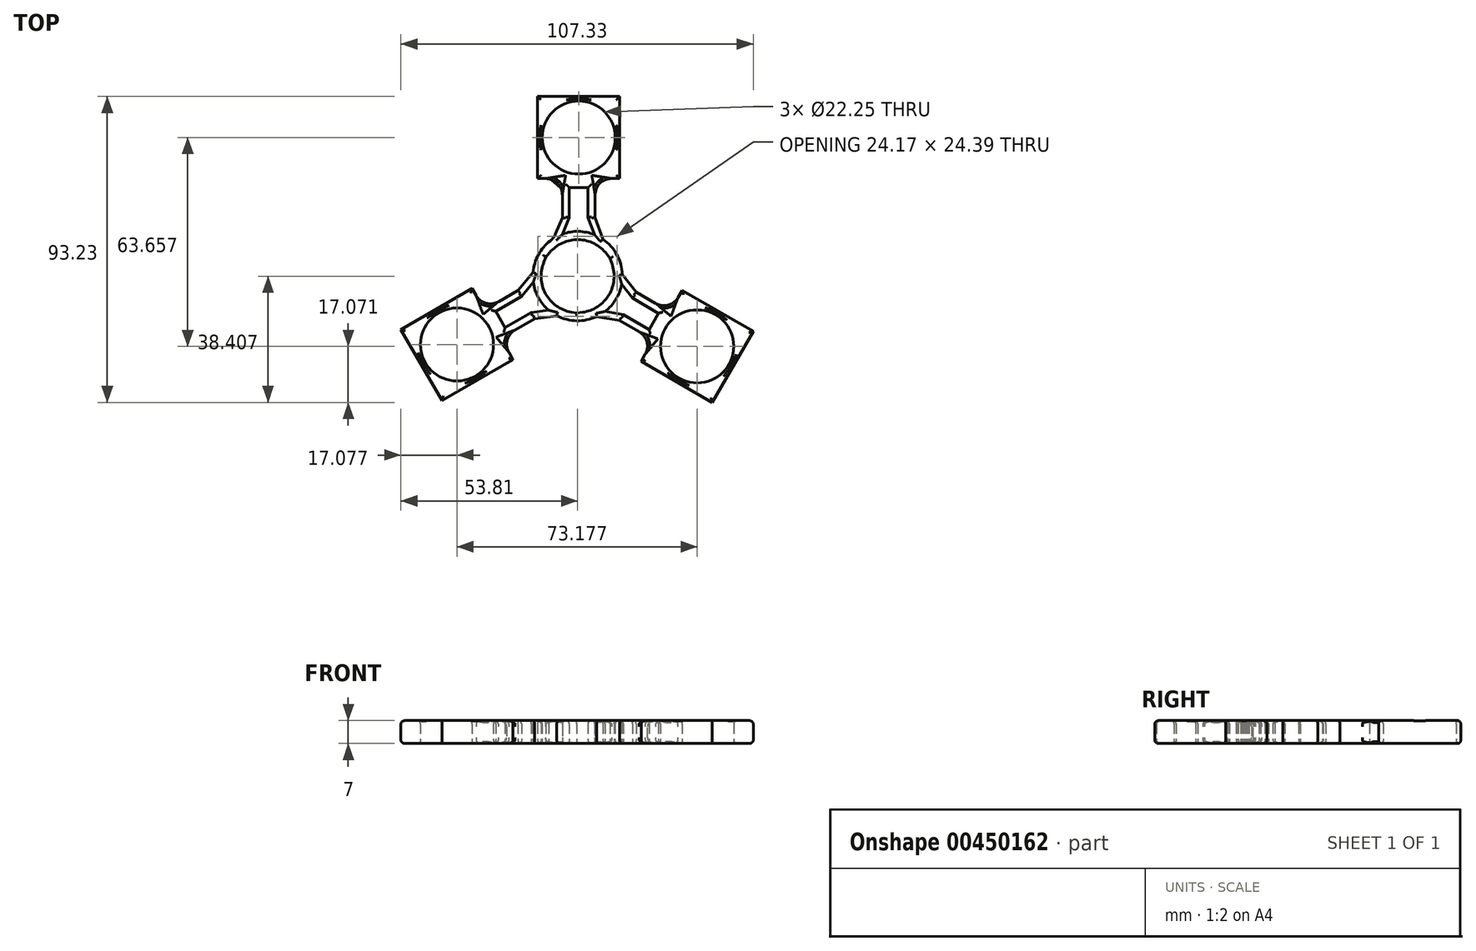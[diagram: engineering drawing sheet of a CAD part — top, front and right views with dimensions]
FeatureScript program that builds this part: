
annotation { "Feature Type Name" : "Feature", "Feature Type Description" : "" }
export const myFeature = defineFeature(function(context is Context, id is Id, definition is map)
    precondition{}
    {
        {
            var Q0;
            Q0=qCreatedBy(makeId("Top.planeOp"),FACE);
            var sketch = newSketch(context, id + "F0", { "sketchPlane" : qUnion([Q0])});
            skCircle(sketch, "E0", {"center": v(0, 0) * mm, "radius": 11.13 * mm});
            skCircle(sketch, "E1.0.1.0", {"center": v(0.33, 42.25) * mm, "radius": 11.13 * mm});
            skLineSegment(sketch, "E2.bottom", {"start": v(12.83, 54.75) * mm, "end": v(-12.17, 54.75) * mm});
            skLineSegment(sketch, "E2.top", {"start": v(12.83, 29.75) * mm, "end": v(-12.17, 29.75) * mm});
            skLineSegment(sketch, "E2.left", {"start": v(12.83, 54.75) * mm, "end": v(12.83, 29.75) * mm});
            skLineSegment(sketch, "E2.right", {"start": v(-12.17, 54.75) * mm, "end": v(-12.17, 29.75) * mm});
            skLineSegment(sketch, "E3", {"start": v(-4.67, 29.75) * mm, "end": v(-4.67, 17.87) * mm});
            skLineSegment(sketch, "E4", {"start": v(-4.67, 17.87) * mm, "end": v(-10.29, 4.24) * mm});
            skLineSegment(sketch, "E5", {"start": v(5.33, 29.75) * mm, "end": v(5.33, 17.9) * mm});
            skLineSegment(sketch, "E6", {"start": v(5.33, 17.9) * mm, "end": v(10.45, 3.8) * mm});
            skLineSegment(sketch, "E7", {"start": v(-2.54, 27) * mm, "end": v(-2.54, 17.8) * mm});
            skLineSegment(sketch, "E8", {"start": v(-2.54, 17.8) * mm, "end": v(-4.82, 12.26) * mm});
            skLineSegment(sketch, "E9", {"start": v(5.25, 12.26) * mm, "end": v(3.2, 17.9) * mm});
            skLineSegment(sketch, "E10", {"start": v(3.2, 17.9) * mm, "end": v(3.2, 27) * mm});
            skLineSegment(sketch, "E11", {"start": v(3.2, 27) * mm, "end": v(-2.54, 27) * mm});
            skCircle(sketch, "E12", {"center": v(0, 0) * mm, "radius": 13.63 * mm});
            skCircle(sketch, "E13.1.0", {"center": v(-36.75, -20.84) * mm, "radius": 11.13 * mm});
            skLineSegment(sketch, "E13.1.1", {"start": v(-28.43, -10.26) * mm, "end": v(-18.16, -4.33) * mm});
            skLineSegment(sketch, "E13.1.2", {"start": v(-32.18, -3.76) * mm, "end": v(-19.68, -25.42) * mm});
            skLineSegment(sketch, "E13.1.3", {"start": v(-53.83, -16.26) * mm, "end": v(-32.18, -3.76) * mm});
            skLineSegment(sketch, "E13.1.4", {"start": v(-41.33, -37.92) * mm, "end": v(-19.68, -25.42) * mm});
            skLineSegment(sketch, "E13.1.5", {"start": v(-53.83, -16.26) * mm, "end": v(-41.33, -37.92) * mm});
            skLineSegment(sketch, "E13.1.6", {"start": v(-22.11, -15.7) * mm, "end": v(-14.15, -11.1) * mm});
            skLineSegment(sketch, "E13.1.7", {"start": v(-17.1, -6.18) * mm, "end": v(-24.98, -10.73) * mm});
            skLineSegment(sketch, "E13.1.8", {"start": v(-24.98, -10.73) * mm, "end": v(-22.11, -15.7) * mm});
            skLineSegment(sketch, "E13.1.9", {"start": v(-13.24, -1.58) * mm, "end": v(-17.1, -6.18) * mm});
            skLineSegment(sketch, "E13.1.10", {"start": v(-14.15, -11.1) * mm, "end": v(-8.2, -10.3) * mm});
            skLineSegment(sketch, "E13.1.12", {"start": v(-13.14, -12.98) * mm, "end": v(1.47, -11.03) * mm});
            skLineSegment(sketch, "E13.1.13", {"start": v(-18.16, -4.33) * mm, "end": v(-8.52, 7.15) * mm});
            skLineSegment(sketch, "E13.1.14", {"start": v(-23.43, -18.92) * mm, "end": v(-13.14, -12.98) * mm});
            skCircle(sketch, "E13.2.0", {"center": v(36.42, -21.4) * mm, "radius": 11.13 * mm});
            skLineSegment(sketch, "E13.2.1", {"start": v(23.1, -19.49) * mm, "end": v(12.84, -13.56) * mm});
            skLineSegment(sketch, "E13.2.2", {"start": v(19.35, -25.98) * mm, "end": v(31.85, -4.33) * mm});
            skLineSegment(sketch, "E13.2.3", {"start": v(41, -38.48) * mm, "end": v(19.35, -25.98) * mm});
            skLineSegment(sketch, "E13.2.4", {"start": v(53.5, -16.83) * mm, "end": v(31.85, -4.33) * mm});
            skLineSegment(sketch, "E13.2.5", {"start": v(41, -38.48) * mm, "end": v(53.5, -16.83) * mm});
            skLineSegment(sketch, "E13.2.6", {"start": v(24.65, -11.3) * mm, "end": v(16.69, -6.7) * mm});
            skLineSegment(sketch, "E13.2.7", {"start": v(13.9, -11.72) * mm, "end": v(21.78, -16.27) * mm});
            skLineSegment(sketch, "E13.2.8", {"start": v(21.78, -16.27) * mm, "end": v(24.65, -11.3) * mm});
            skLineSegment(sketch, "E13.2.9", {"start": v(8, -10.68) * mm, "end": v(13.9, -11.72) * mm});
            skLineSegment(sketch, "E13.2.10", {"start": v(16.69, -6.7) * mm, "end": v(13.03, -1.96) * mm});
            skLineSegment(sketch, "E13.2.12", {"start": v(17.81, -4.9) * mm, "end": v(8.81, 6.8) * mm});
            skLineSegment(sketch, "E13.2.13", {"start": v(12.84, -13.56) * mm, "end": v(-1.93, -10.96) * mm});
            skLineSegment(sketch, "E13.2.14", {"start": v(28.1, -10.83) * mm, "end": v(17.81, -4.9) * mm});
            skSolve(sketch);
        }
        {
            var Q0;
            Q0 = qSketchRegion(id + "F0", true);
            extrude(context, id + "F1", {"entities" : qUnion([Q0]), "depth" : 7 * mm, "offsetDistance" : 25 * mm});
        }
        {
            var Q0;
            Q0=makeQuery(id+"F1.opExtrude","SWEPT_EDGE",EDGE,{"disambiguationData":[OSD([sQuery(id+"F0.wireOp",EDGE,"E4"),sQuery(id+"F0.wireOp",EDGE,"E12")])]});
            fillet(context, id + "F2", {"entities" : qUnion([Q0]), "radius" : 5 * mm, "tangentPropagation" : true, "allowEdgeOverflow" : false});
        }
        {
            var Q0;
            Q0=makeQuery(id+"F1.opExtrude","CAP_FACE",FACE,{"disambiguationData":[OSD([sQuery(id+"F0.wireOp",EDGE,"E0"),sQuery(id+"F0.wireOp",EDGE,"E1.0.1.0"),sQuery(id+"F0.wireOp",EDGE,"E2.bottom"),sQuery(id+"F0.wireOp",EDGE,"E2.top"),sQuery(id+"F0.wireOp",EDGE,"E2.left"),sQuery(id+"F0.wireOp",EDGE,"E2.right"),sQuery(id+"F0.wireOp",EDGE,"E3"),sQuery(id+"F0.wireOp",EDGE,"E4"),sQuery(id+"F0.wireOp",EDGE,"E5"),sQuery(id+"F0.wireOp",EDGE,"E6"),sQuery(id+"F0.wireOp",EDGE,"E7"),sQuery(id+"F0.wireOp",EDGE,"E8"),sQuery(id+"F0.wireOp",EDGE,"E9"),sQuery(id+"F0.wireOp",EDGE,"E10"),sQuery(id+"F0.wireOp",EDGE,"E11"),sQuery(id+"F0.wireOp",EDGE,"E12"),sQuery(id+"F0.wireOp",EDGE,"E13.1.0"),sQuery(id+"F0.wireOp",EDGE,"E13.1.1"),sQuery(id+"F0.wireOp",EDGE,"E13.1.2"),sQuery(id+"F0.wireOp",EDGE,"E13.1.3"),sQuery(id+"F0.wireOp",EDGE,"E13.1.4"),sQuery(id+"F0.wireOp",EDGE,"E13.1.5"),sQuery(id+"F0.wireOp",EDGE,"E13.1.6"),sQuery(id+"F0.wireOp",EDGE,"E13.1.7"),sQuery(id+"F0.wireOp",EDGE,"E13.1.8"),sQuery(id+"F0.wireOp",EDGE,"E13.1.9"),sQuery(id+"F0.wireOp",EDGE,"E13.1.10"),sQuery(id+"F0.wireOp",EDGE,"E13.1.12"),sQuery(id+"F0.wireOp",EDGE,"E13.1.13"),sQuery(id+"F0.wireOp",EDGE,"E13.1.14"),sQuery(id+"F0.wireOp",EDGE,"E13.2.0"),sQuery(id+"F0.wireOp",EDGE,"E13.2.1"),sQuery(id+"F0.wireOp",EDGE,"E13.2.2"),sQuery(id+"F0.wireOp",EDGE,"E13.2.3"),sQuery(id+"F0.wireOp",EDGE,"E13.2.4"),sQuery(id+"F0.wireOp",EDGE,"E13.2.5"),sQuery(id+"F0.wireOp",EDGE,"E13.2.6"),sQuery(id+"F0.wireOp",EDGE,"E13.2.7"),sQuery(id+"F0.wireOp",EDGE,"E13.2.8"),sQuery(id+"F0.wireOp",EDGE,"E13.2.9"),sQuery(id+"F0.wireOp",EDGE,"E13.2.10"),sQuery(id+"F0.wireOp",EDGE,"E13.2.12"),sQuery(id+"F0.wireOp",EDGE,"E13.2.13"),sQuery(id+"F0.wireOp",EDGE,"E13.2.14")])],"isStart":false});
            fillet(context, id + "F3", {"entities" : qUnion([Q0]), "radius" : 1 * mm, "tangentPropagation" : true, "allowEdgeOverflow" : false});
        }
        {
            var Q0;
            Q0=makeQuery(id+"F1.opExtrude","CAP_FACE",FACE,{"disambiguationData":[OSD([sQuery(id+"F0.wireOp",EDGE,"E0"),sQuery(id+"F0.wireOp",EDGE,"E1.0.1.0"),sQuery(id+"F0.wireOp",EDGE,"E2.bottom"),sQuery(id+"F0.wireOp",EDGE,"E2.top"),sQuery(id+"F0.wireOp",EDGE,"E2.left"),sQuery(id+"F0.wireOp",EDGE,"E2.right"),sQuery(id+"F0.wireOp",EDGE,"E3"),sQuery(id+"F0.wireOp",EDGE,"E4"),sQuery(id+"F0.wireOp",EDGE,"E5"),sQuery(id+"F0.wireOp",EDGE,"E6"),sQuery(id+"F0.wireOp",EDGE,"E7"),sQuery(id+"F0.wireOp",EDGE,"E8"),sQuery(id+"F0.wireOp",EDGE,"E9"),sQuery(id+"F0.wireOp",EDGE,"E10"),sQuery(id+"F0.wireOp",EDGE,"E11"),sQuery(id+"F0.wireOp",EDGE,"E12"),sQuery(id+"F0.wireOp",EDGE,"E13.1.0"),sQuery(id+"F0.wireOp",EDGE,"E13.1.1"),sQuery(id+"F0.wireOp",EDGE,"E13.1.2"),sQuery(id+"F0.wireOp",EDGE,"E13.1.3"),sQuery(id+"F0.wireOp",EDGE,"E13.1.4"),sQuery(id+"F0.wireOp",EDGE,"E13.1.5"),sQuery(id+"F0.wireOp",EDGE,"E13.1.6"),sQuery(id+"F0.wireOp",EDGE,"E13.1.7"),sQuery(id+"F0.wireOp",EDGE,"E13.1.8"),sQuery(id+"F0.wireOp",EDGE,"E13.1.9"),sQuery(id+"F0.wireOp",EDGE,"E13.1.10"),sQuery(id+"F0.wireOp",EDGE,"E13.1.12"),sQuery(id+"F0.wireOp",EDGE,"E13.1.13"),sQuery(id+"F0.wireOp",EDGE,"E13.1.14"),sQuery(id+"F0.wireOp",EDGE,"E13.2.0"),sQuery(id+"F0.wireOp",EDGE,"E13.2.1"),sQuery(id+"F0.wireOp",EDGE,"E13.2.2"),sQuery(id+"F0.wireOp",EDGE,"E13.2.3"),sQuery(id+"F0.wireOp",EDGE,"E13.2.4"),sQuery(id+"F0.wireOp",EDGE,"E13.2.5"),sQuery(id+"F0.wireOp",EDGE,"E13.2.6"),sQuery(id+"F0.wireOp",EDGE,"E13.2.7"),sQuery(id+"F0.wireOp",EDGE,"E13.2.8"),sQuery(id+"F0.wireOp",EDGE,"E13.2.9"),sQuery(id+"F0.wireOp",EDGE,"E13.2.10"),sQuery(id+"F0.wireOp",EDGE,"E13.2.12"),sQuery(id+"F0.wireOp",EDGE,"E13.2.13"),sQuery(id+"F0.wireOp",EDGE,"E13.2.14")])],"isStart":true});
            fillet(context, id + "F4", {"entities" : qUnion([Q0]), "radius" : 1 * mm, "tangentPropagation" : true, "allowEdgeOverflow" : false});
        }
        {
            var Q0;
            Q0=makeQuery(id+"F1.opExtrude","SWEPT_EDGE",EDGE,{"disambiguationData":[OSD([sQuery(id+"F0.wireOp",EDGE,"E13.1.2"),sQuery(id+"F0.wireOp",EDGE,"E13.1.14")])]});
            var Q1;
            Q1=makeQuery(id+"F1.opExtrude","SWEPT_EDGE",EDGE,{"disambiguationData":[OSD([sQuery(id+"F0.wireOp",EDGE,"E13.1.1"),sQuery(id+"F0.wireOp",EDGE,"E13.1.2")])]});
            var Q2;
            Q2=makeQuery(id+"F1.opExtrude","SWEPT_EDGE",EDGE,{"disambiguationData":[OSD([sQuery(id+"F0.wireOp",EDGE,"E2.top"),sQuery(id+"F0.wireOp",EDGE,"E5")])]});
            var Q3;
            Q3=makeQuery(id+"F1.opExtrude","SWEPT_EDGE",EDGE,{"disambiguationData":[OSD([sQuery(id+"F0.wireOp",EDGE,"E2.top"),sQuery(id+"F0.wireOp",EDGE,"E3")])]});
            var Q4;
            Q4=makeQuery(id+"F1.opExtrude","SWEPT_EDGE",EDGE,{"disambiguationData":[OSD([sQuery(id+"F0.wireOp",EDGE,"E13.2.1"),sQuery(id+"F0.wireOp",EDGE,"E13.2.2")])]});
            var Q5;
            Q5=makeQuery(id+"F1.opExtrude","SWEPT_EDGE",EDGE,{"disambiguationData":[OSD([sQuery(id+"F0.wireOp",EDGE,"E13.2.2"),sQuery(id+"F0.wireOp",EDGE,"E13.2.14")])]});
            fillet(context, id + "F5", {"entities" : qUnion([Q0, Q1, Q2, Q3, Q4, Q5]), "radius" : 5 * mm, "tangentPropagation" : true, "allowEdgeOverflow" : false});
        }
    });
